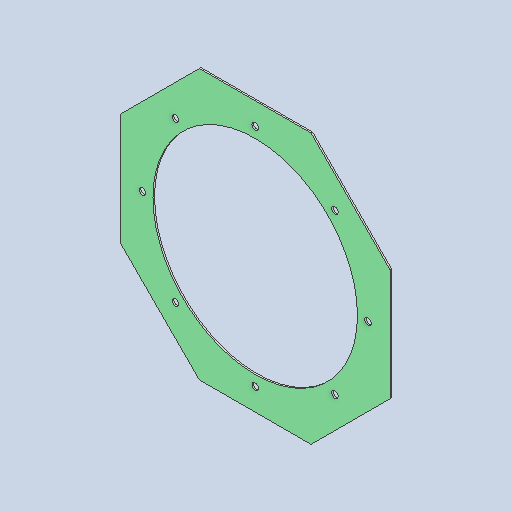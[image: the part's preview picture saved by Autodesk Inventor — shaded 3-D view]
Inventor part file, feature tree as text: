
AUTODESK INVENTOR PART (.ipt)
format: ipt  version: 2025 (Build 290162010, 162A)  size: 159,744 bytes
history: native  units: mm
features: sketch x2, other x2, sheet_metal_op x1, extrude x1, pattern_circular x1
ambient origin geometry x8: Origin, YZ Plane, XZ Plane, XY Plane, X Axis, Y Axis, Z Axis, Center Point
bodies: Solid1 (feature_tree)
feature tree (7):
  sheet_metal_op  "Face1"
  extrude  "Extrusion1"  Depth=3.0mm
  pattern_circular  "Circular Pattern1"  [2 undecoded]
  sketch  "Sketch2"  dims[d15=3.0mm d16=12.5mm]
  other  "Plate1"
  sketch  "Sketch4"  dims[d17=214.5mm d18=10.0mm d19=0.0mm d20=80.0mm d21=360.0deg d23=513.0mm d26=389.0mm]
  other  "Definition1"
note: 2 required parameter values undecoded (feature->parameter linkage not recoverable at this tier; creation-order binding heuristic only, values carry confidence <= 0.55)
